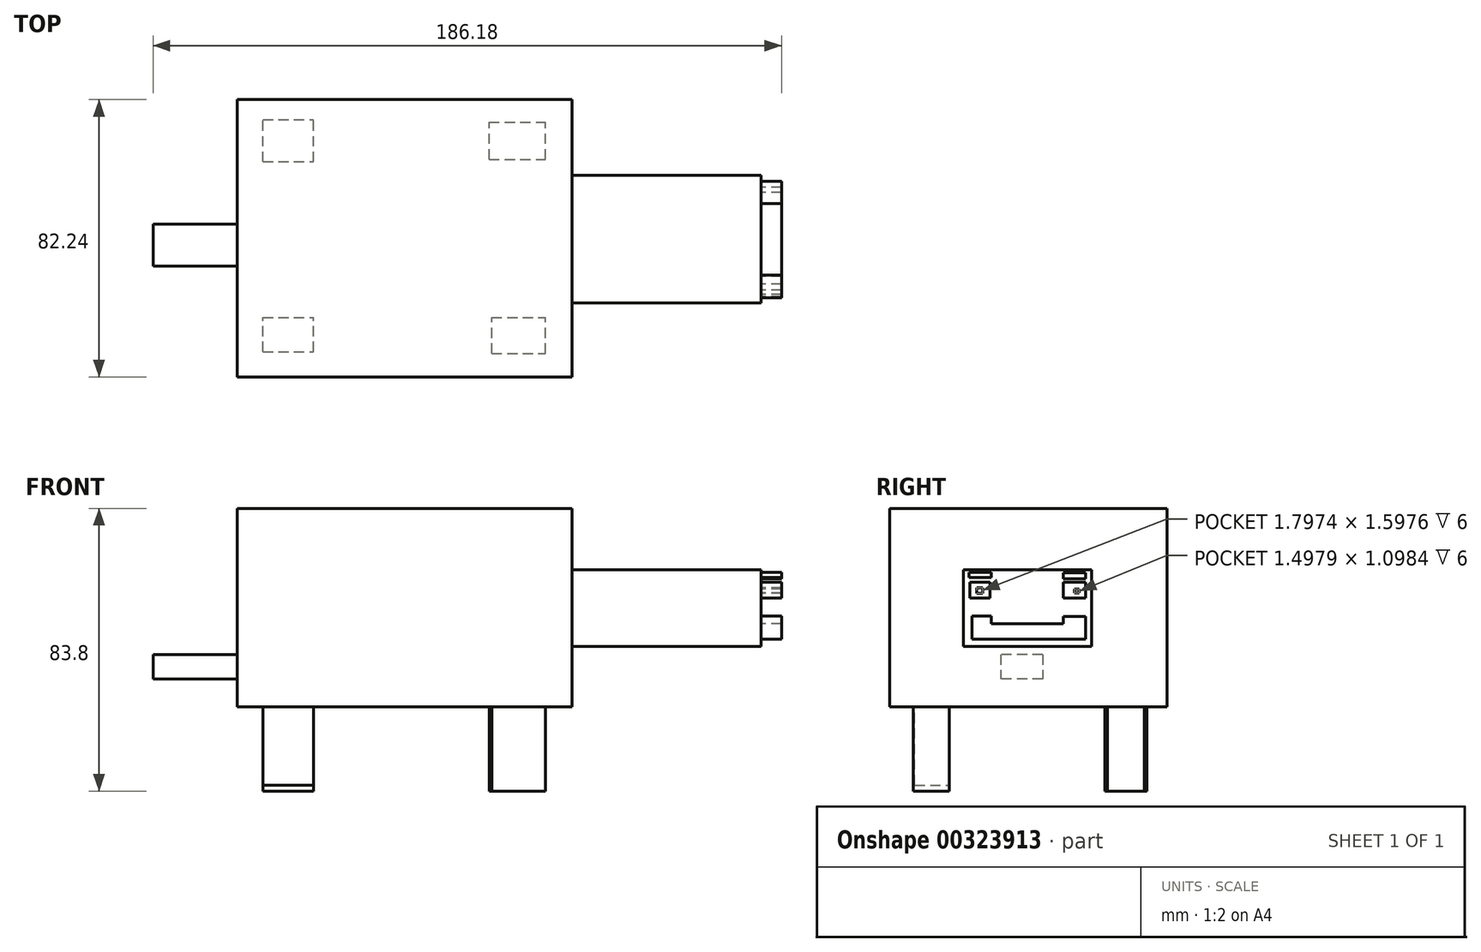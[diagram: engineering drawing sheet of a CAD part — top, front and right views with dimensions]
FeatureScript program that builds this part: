
annotation { "Feature Type Name" : "Feature", "Feature Type Description" : "" }
export const myFeature = defineFeature(function(context is Context, id is Id, definition is map)
    precondition{}
    {
        {
            var Q0;
            Q0=qCreatedBy(makeId("Top.planeOp"),FACE);
            var sketch = newSketch(context, id + "F0", { "sketchPlane" : qUnion([Q0])});
            skLineSegment(sketch, "E0.bottom", {"start": v(-49.1, 43.86) * mm, "end": v(50.1, 43.86) * mm});
            skLineSegment(sketch, "E0.top", {"start": v(-49.1, -38.38) * mm, "end": v(50.1, -38.38) * mm});
            skLineSegment(sketch, "E0.left", {"start": v(-49.1, 43.86) * mm, "end": v(-49.1, -38.38) * mm});
            skLineSegment(sketch, "E0.right", {"start": v(50.1, 43.86) * mm, "end": v(50.1, -38.38) * mm});
            skSolve(sketch);
        }
        {
            var Q0;
            Q0 = qSketchRegion(id + "F0", true);
            extrude(context, id + "F1", {"entities" : qUnion([Q0]), "depth" : 58.8 * mm});
        }
        {
            var Q0;
            Q0=makeQuery(id+"F1.opExtrude","SWEPT_FACE",FACE,{"disambiguationData":[OSD([sQuery(id+"F0.wireOp",EDGE,"E0.right")])]});
            var sketch = newSketch(context, id + "F2", { "sketchPlane" : qUnion([Q0])});
            skLineSegment(sketch, "E1.bottom", {"start": v(-16.45, 40.62) * mm, "end": v(21.43, 40.62) * mm});
            skLineSegment(sketch, "E1.top", {"start": v(-16.45, 17.94) * mm, "end": v(21.43, 17.94) * mm});
            skLineSegment(sketch, "E1.left", {"start": v(-16.45, 40.62) * mm, "end": v(-16.45, 17.94) * mm});
            skLineSegment(sketch, "E1.right", {"start": v(21.43, 40.62) * mm, "end": v(21.43, 17.94) * mm});
            skSolve(sketch);
        }
        {
            var Q0;
            Q0 = qSketchRegion(id + "F2", true);
            extrude(context, id + "F3", {"entities" : qUnion([Q0]), "operationType" : NewBodyOperationType.ADD, "depth" : 53 * mm});
        }
        {
            var Q0;
            Q0=makeQuery(id+"F1.opExtrude","CAP_FACE",FACE,{"disambiguationData":[OSD([sQuery(id+"F0.wireOp",EDGE,"E0.bottom"),sQuery(id+"F0.wireOp",EDGE,"E0.top"),sQuery(id+"F0.wireOp",EDGE,"E0.left"),sQuery(id+"F0.wireOp",EDGE,"E0.right")])],"isStart":true});
            var sketch = newSketch(context, id + "F4", { "sketchPlane" : qUnion([Q0])});
            skLineSegment(sketch, "E2.bottom", {"start": v(-41.53, 30.9) * mm, "end": v(-26.58, 30.9) * mm});
            skLineSegment(sketch, "E2.top", {"start": v(-41.53, 20.68) * mm, "end": v(-26.58, 20.68) * mm});
            skLineSegment(sketch, "E2.left", {"start": v(-41.53, 30.9) * mm, "end": v(-41.53, 20.68) * mm});
            skLineSegment(sketch, "E2.right", {"start": v(-26.58, 30.9) * mm, "end": v(-26.58, 20.68) * mm});
            skSolve(sketch);
        }
        {
            var Q0;
            Q0 = qSketchRegion(id + "F4", true);
            extrude(context, id + "F5", {"entities" : qUnion([Q0]), "operationType" : NewBodyOperationType.ADD, "depth" : 23.2 * mm});
        }
        {
            var Q0;
            Q0=makeQuery(id+"F1.opExtrude","CAP_FACE",FACE,{"disambiguationData":[OSD([sQuery(id+"F0.wireOp",EDGE,"E0.bottom"),sQuery(id+"F0.wireOp",EDGE,"E0.top"),sQuery(id+"F0.wireOp",EDGE,"E0.left"),sQuery(id+"F0.wireOp",EDGE,"E0.right")])],"isStart":true});
            var sketch = newSketch(context, id + "F6", { "sketchPlane" : qUnion([Q0])});
            skLineSegment(sketch, "E3.bottom", {"start": v(26.26, 31.4) * mm, "end": v(42.2, 31.4) * mm});
            skLineSegment(sketch, "E3.top", {"start": v(26.26, 20.68) * mm, "end": v(42.2, 20.68) * mm});
            skLineSegment(sketch, "E3.left", {"start": v(26.26, 31.4) * mm, "end": v(26.26, 20.68) * mm});
            skLineSegment(sketch, "E3.right", {"start": v(42.2, 31.4) * mm, "end": v(42.2, 20.68) * mm});
            skLineSegment(sketch, "E4.bottom", {"start": v(25.5, -26.17) * mm, "end": v(42.2, -26.17) * mm});
            skLineSegment(sketch, "E4.top", {"start": v(25.5, -37.13) * mm, "end": v(42.2, -37.13) * mm});
            skLineSegment(sketch, "E4.left", {"start": v(25.5, -26.17) * mm, "end": v(25.5, -37.13) * mm});
            skLineSegment(sketch, "E4.right", {"start": v(42.2, -26.17) * mm, "end": v(42.2, -37.13) * mm});
            skLineSegment(sketch, "E5.bottom", {"start": v(-41.53, -25.42) * mm, "end": v(-26.58, -25.42) * mm});
            skLineSegment(sketch, "E5.top", {"start": v(-41.53, -37.88) * mm, "end": v(-26.58, -37.88) * mm});
            skLineSegment(sketch, "E5.left", {"start": v(-41.53, -25.42) * mm, "end": v(-41.53, -37.88) * mm});
            skLineSegment(sketch, "E5.right", {"start": v(-26.58, -25.42) * mm, "end": v(-26.58, -37.88) * mm});
            skSolve(sketch);
        }
        {
            var Q0;
            Q0 = qSketchRegion(id + "F6", true);
            extrude(context, id + "F7", {"entities" : qUnion([Q0]), "operationType" : NewBodyOperationType.ADD, "depth" : 25 * mm});
        }
        {
            var Q0;
            Q0=makeQuery(id+"F3.opExtrude","CAP_FACE",FACE,{"disambiguationData":[OSD([sQuery(id+"F2.wireOp",EDGE,"E1.bottom"),sQuery(id+"F2.wireOp",EDGE,"E1.top"),sQuery(id+"F2.wireOp",EDGE,"E1.left"),sQuery(id+"F2.wireOp",EDGE,"E1.right")])],"isStart":false});
            var sketch = newSketch(context, id + "F8", { "sketchPlane" : qUnion([Q0])});
            skSolve(sketch);
        }
        {
            var Q0;
            Q0=makeQuery(id+"F8.imprint","IMPRINT",FACE,{"disambiguationData":[TD([[makeQuery(id+"F8.imprint","IMPRINT",EDGE,{"derivedFrom":makeQuery(id+"F3.opExtrude","CAP_EDGE",EDGE,{"disambiguationData":[OSD([sQuery(id+"F2.wireOp",EDGE,"E1.bottom")])],"isStart":false})}),-1.0]])]});
            extrude(context, id + "F9", {"entities" : qUnion([Q0]), "operationType" : NewBodyOperationType.ADD, "depth" : 3 * mm});
        }
        {
            var Q0;
            Q0=makeQuery(id+"F9.opExtrude","CAP_FACE",FACE,{"disambiguationData":[OSD([sQuery(id+"F2.wireOp",EDGE,"E1.bottom"),sQuery(id+"F2.wireOp",EDGE,"E1.top"),sQuery(id+"F2.wireOp",EDGE,"E1.left"),sQuery(id+"F2.wireOp",EDGE,"E1.right")])],"isStart":false});
            var sketch = newSketch(context, id + "F10", { "sketchPlane" : qUnion([Q0])});
            skLineSegment(sketch, "E6.bottom", {"start": v(-14.58, 36.89) * mm, "end": v(-8.6, 36.89) * mm});
            skLineSegment(sketch, "E6.top", {"start": v(-14.58, 32.2) * mm, "end": v(-8.6, 32.2) * mm});
            skLineSegment(sketch, "E6.left", {"start": v(-14.58, 36.89) * mm, "end": v(-14.58, 32.2) * mm});
            skLineSegment(sketch, "E6.right", {"start": v(-8.6, 36.89) * mm, "end": v(-8.6, 32.2) * mm});
            skLineSegment(sketch, "E7.bottom", {"start": v(13.08, 36.89) * mm, "end": v(19.67, 36.89) * mm});
            skLineSegment(sketch, "E7.top", {"start": v(13.08, 32.2) * mm, "end": v(19.67, 32.2) * mm});
            skLineSegment(sketch, "E7.left", {"start": v(13.08, 36.89) * mm, "end": v(13.08, 32.2) * mm});
            skLineSegment(sketch, "E7.right", {"start": v(19.67, 36.89) * mm, "end": v(19.67, 32.2) * mm});
            skLineSegment(sketch, "E8.bottom", {"start": v(-13.88, 26.9) * mm, "end": v(-8.2, 26.9) * mm});
            skLineSegment(sketch, "E8.top", {"start": v(-13.88, 20.11) * mm, "end": v(-8.2, 20.11) * mm});
            skLineSegment(sketch, "E8.left", {"start": v(-13.88, 26.9) * mm, "end": v(-13.88, 20.11) * mm});
            skLineSegment(sketch, "E8.right", {"start": v(-8.2, 26.9) * mm, "end": v(-8.2, 20.11) * mm});
            skLineSegment(sketch, "E9.bottom", {"start": v(-13.88, 20.11) * mm, "end": v(19.67, 20.11) * mm});
            skLineSegment(sketch, "E9.top", {"start": v(-13.88, 24.6) * mm, "end": v(19.67, 24.6) * mm});
            skLineSegment(sketch, "E9.left", {"start": v(-13.88, 20.11) * mm, "end": v(-13.88, 24.6) * mm});
            skLineSegment(sketch, "E9.right", {"start": v(19.67, 20.11) * mm, "end": v(19.67, 24.6) * mm});
            skLineSegment(sketch, "E10.bottom", {"start": v(19.67, 20.11) * mm, "end": v(13.08, 20.11) * mm});
            skLineSegment(sketch, "E10.top", {"start": v(19.67, 26.8) * mm, "end": v(13.08, 26.8) * mm});
            skLineSegment(sketch, "E10.left", {"start": v(19.67, 20.11) * mm, "end": v(19.67, 26.8) * mm});
            skLineSegment(sketch, "E10.right", {"start": v(13.08, 20.11) * mm, "end": v(13.08, 26.8) * mm});
            skLineSegment(sketch, "E11.bottom", {"start": v(-14.88, 39.88) * mm, "end": v(-8.2, 39.88) * mm});
            skLineSegment(sketch, "E11.top", {"start": v(-14.88, 38.29) * mm, "end": v(-8.2, 38.29) * mm});
            skLineSegment(sketch, "E11.left", {"start": v(-14.88, 39.88) * mm, "end": v(-14.88, 38.29) * mm});
            skLineSegment(sketch, "E11.right", {"start": v(-8.2, 39.88) * mm, "end": v(-8.2, 38.29) * mm});
            skLineSegment(sketch, "E12.bottom", {"start": v(13.08, 39.68) * mm, "end": v(19.67, 39.68) * mm});
            skLineSegment(sketch, "E12.top", {"start": v(13.08, 37.99) * mm, "end": v(19.67, 37.99) * mm});
            skLineSegment(sketch, "E12.left", {"start": v(13.08, 39.68) * mm, "end": v(13.08, 37.99) * mm});
            skLineSegment(sketch, "E12.right", {"start": v(19.67, 39.68) * mm, "end": v(19.67, 37.99) * mm});
            skLineSegment(sketch, "E13.bottom", {"start": v(-12.59, 35.3) * mm, "end": v(-10.79, 35.3) * mm});
            skLineSegment(sketch, "E13.top", {"start": v(-12.59, 33.7) * mm, "end": v(-10.79, 33.7) * mm});
            skLineSegment(sketch, "E13.left", {"start": v(-12.59, 35.3) * mm, "end": v(-12.59, 33.7) * mm});
            skLineSegment(sketch, "E13.right", {"start": v(-10.79, 35.3) * mm, "end": v(-10.79, 33.7) * mm});
            skPoint(sketch, "E14.firstSnap0", {"position": v(16.37, 36.89) * mm});
            skLineSegment(sketch, "E14.bottom", {"start": v(16.37, 34.9) * mm, "end": v(17.87, 34.9) * mm});
            skLineSegment(sketch, "E14.top", {"start": v(16.37, 33.8) * mm, "end": v(17.87, 33.8) * mm});
            skLineSegment(sketch, "E14.left", {"start": v(16.37, 34.9) * mm, "end": v(16.37, 33.8) * mm});
            skLineSegment(sketch, "E14.right", {"start": v(17.87, 34.9) * mm, "end": v(17.87, 33.8) * mm});
            skSolve(sketch);
        }
        {
            var Q0;
            Q0 = qSketchRegion(id + "F10", true);
            extrude(context, id + "F11", {"entities" : qUnion([Q0]), "operationType" : NewBodyOperationType.ADD, "depth" : 6 * mm});
        }
        {
            var Q0;
            Q0=makeQuery(id+"F1.opExtrude","SWEPT_FACE",FACE,{"disambiguationData":[OSD([sQuery(id+"F0.wireOp",EDGE,"E0.left")])]});
            var sketch = newSketch(context, id + "F12", { "sketchPlane" : qUnion([Q0])});
            skLineSegment(sketch, "E15.bottom", {"start": v(-6.98, 15.45) * mm, "end": v(5.48, 15.45) * mm});
            skLineSegment(sketch, "E15.top", {"start": v(-6.98, 8.22) * mm, "end": v(5.48, 8.22) * mm});
            skLineSegment(sketch, "E15.left", {"start": v(-6.98, 15.45) * mm, "end": v(-6.98, 8.22) * mm});
            skLineSegment(sketch, "E15.right", {"start": v(5.48, 15.45) * mm, "end": v(5.48, 8.22) * mm});
            skSolve(sketch);
        }
        {
            var Q0;
            Q0 = qSketchRegion(id + "F12", true);
            extrude(context, id + "F13", {"entities" : qUnion([Q0]), "operationType" : NewBodyOperationType.ADD, "depth" : 25 * mm});
        }
    });
